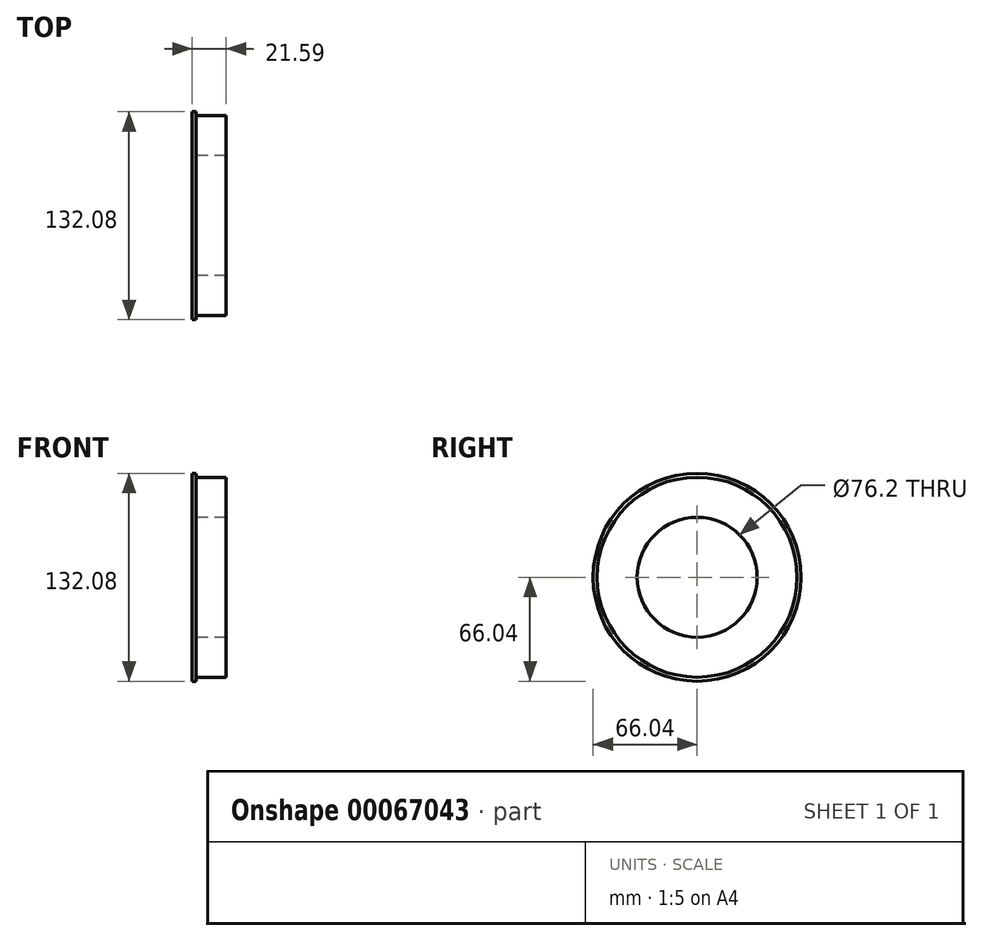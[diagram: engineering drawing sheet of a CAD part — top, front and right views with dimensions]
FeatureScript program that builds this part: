
annotation { "Feature Type Name" : "Feature", "Feature Type Description" : "" }
export const myFeature = defineFeature(function(context is Context, id is Id, definition is map)
    precondition{}
    {
        {
            var Q0;
            Q0=qCreatedBy(makeId("Right.planeOp"),FACE);
            var sketch = newSketch(context, id + "F0", { "sketchPlane" : qUnion([Q0])});
            skCircle(sketch, "E0", {"center": v(0, 0) * mm, "radius": 63.5 * mm});
            skCircle(sketch, "E1", {"center": v(0, 0) * mm, "radius": 38.1 * mm});
            skSolve(sketch);
        }
        {
            var Q0;
            Q0=qSketchRegion(id+"F0",true);
            extrude(context, id + "F1", {"entities" : qUnion([Q0]), "depth" : 19.05 * mm});
        }
        {
            var Q0;
            Q0=makeQuery(id+"F1.opExtrude","CAP_FACE",FACE,{"disambiguationData":[OSD([sQuery(id+"F0.wireOp",EDGE,"E0"),sQuery(id+"F0.wireOp",EDGE,"E1")])],"isStart":true});
            var sketch = newSketch(context, id + "F2", { "sketchPlane" : qUnion([Q0])});
            skCircle(sketch, "E2", {"center": v(0, 0) * mm, "radius": 38.1 * mm});
            skCircle(sketch, "E3", {"center": v(0, 0) * mm, "radius": 66.04 * mm});
            skPoint(sketch, "E4", {"position": v(0, 63.5) * mm});
            skSolve(sketch);
        }
        {
            var Q0;
            Q0=qSketchRegion(id+"F2",true);
            extrude(context, id + "F3", {"entities" : qUnion([Q0]), "operationType" : NewBodyOperationType.ADD, "depth" : 2.54 * mm});
        }
    });
